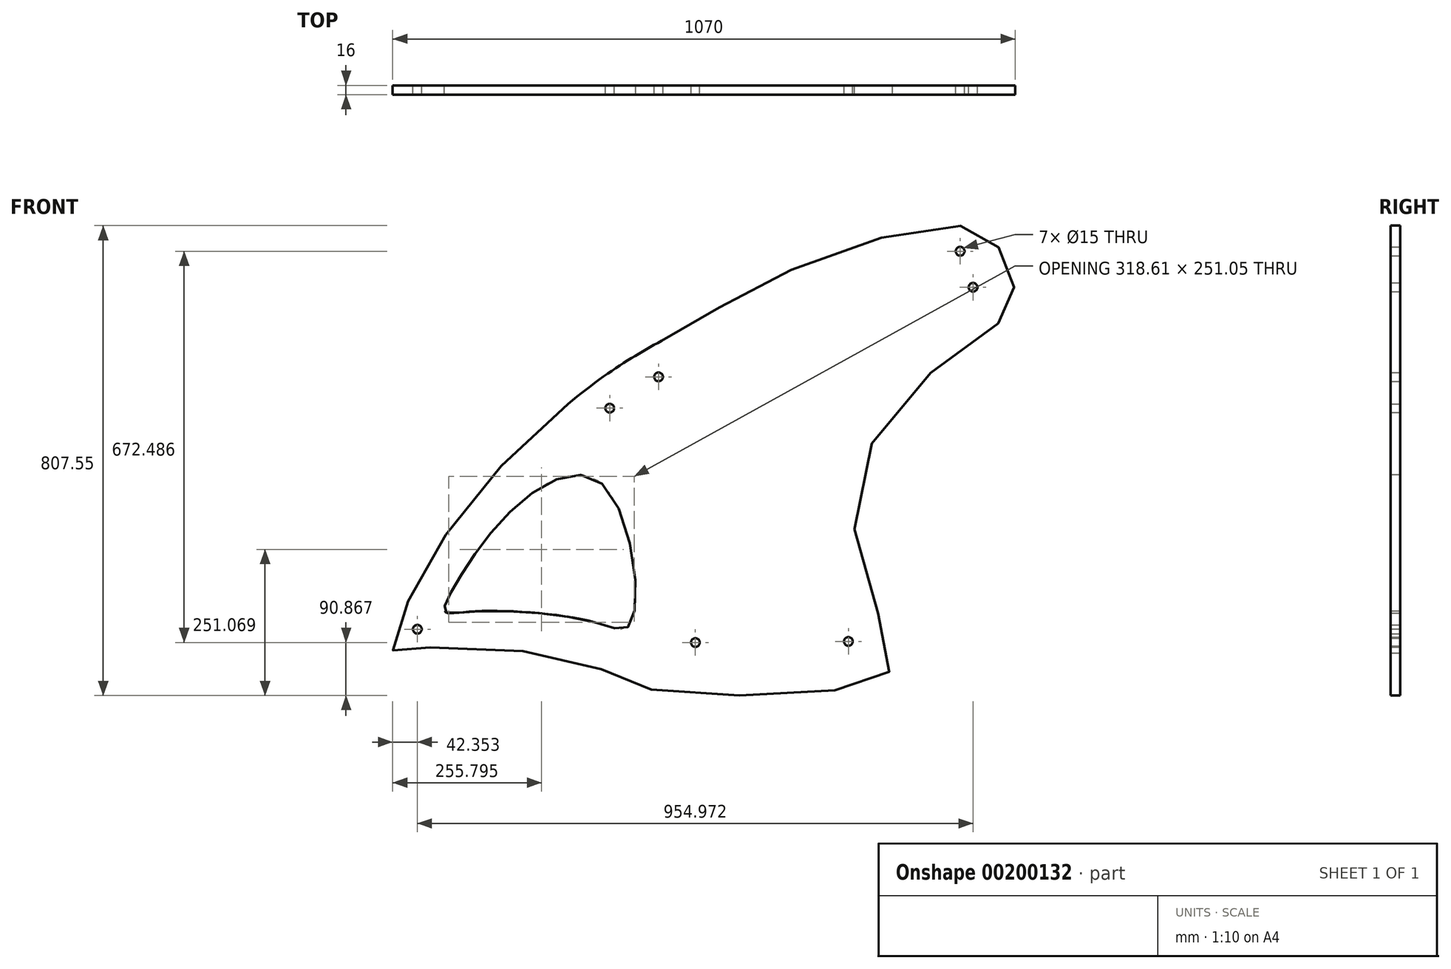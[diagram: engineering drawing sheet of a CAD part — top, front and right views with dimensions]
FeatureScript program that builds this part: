
annotation { "Feature Type Name" : "Feature", "Feature Type Description" : "" }
export const myFeature = defineFeature(function(context is Context, id is Id, definition is map)
    precondition{}
    {
        {
            var Q0;
            Q0=qCreatedBy(makeId("Front.planeOp"),FACE);
            var sketch = newSketch(context, id + "F0", { "sketchPlane" : qUnion([Q0])});
            skFitSpline(sketch, "E0", {"points": [v(296.8, 611.98) * mm, v(322.84, 547.63) * mm, v(318.6, 501.05) * mm, v(130.85, 348.58) * mm, v(56.03, 83.18) * mm, v(113.37, -111.05) * mm, v(0, -152.58) * mm, v(-308.6, -147.46) * mm, v(-413.67, -103.87) * mm, v(-700.28, -79.67) * mm, v(-741.76, -85.2) * mm, v(-720.02, -4.27) * mm, v(-590.43, 197.07) * mm, v(-376.55, 391.5) * mm, v(-238.95, 473.77) * mm, v(-38.49, 580.12) * mm, v(233.92, 647.2) * mm, v(296.8, 611.98) * mm]});
            skFitSpline(sketch, "E1", {"points": [v(-396.1, -34.16) * mm, v(-333.66, -35.6) * mm, v(-383.57, 203.97) * mm, v(-527.62, 168.65) * mm, v(-634.93, 31.23) * mm, v(-653.89, -14.93) * mm, v(-606.14, -15.45) * mm, v(-396.1, -34.16) * mm]});
            skFitSpline(sketch, "E2", {"points": [v(-423.1, 318.98) * mm, v(-514.85, 391.93) * mm, v(-576.24, 405.79) * mm, v(-634.5, 459.84) * mm, v(-484.83, 432.17) * mm, v(-242.1, 440.97) * mm, v(-245.01, 368.92) * mm, v(-319.45, 315.2) * mm, v(-394.83, 283.17) * mm, v(-423.1, 318.98) * mm]});
            skCircle(sketch, "E3", {"center": v(-700.99, -46.02) * mm, "radius": 12.5 * mm});
            skCircle(sketch, "E4", {"center": v(-700.99, -46.02) * mm, "radius": 7.5 * mm});
            skCircle(sketch, "E5", {"center": v(-223.24, -68.84) * mm, "radius": 12.5 * mm});
            skCircle(sketch, "E6", {"center": v(-223.24, -68.84) * mm, "radius": 7.5 * mm});
            skCircle(sketch, "E7", {"center": v(39.8, -66.94) * mm, "radius": 12.5 * mm});
            skCircle(sketch, "E8", {"center": v(39.8, -66.94) * mm, "radius": 7.5 * mm});
            skCircle(sketch, "E9", {"center": v(-370.33, 334.05) * mm, "radius": 12.5 * mm});
            skCircle(sketch, "E10", {"center": v(-370.33, 334.05) * mm, "radius": 7.5 * mm});
            skCircle(sketch, "E11", {"center": v(-286.47, 387.76) * mm, "radius": 12.5 * mm});
            skCircle(sketch, "E12", {"center": v(-286.47, 387.76) * mm, "radius": 7.5 * mm});
            skCircle(sketch, "E13", {"center": v(231.8, 603.64) * mm, "radius": 12.5 * mm});
            skCircle(sketch, "E14", {"center": v(231.8, 603.64) * mm, "radius": 7.5 * mm});
            skCircle(sketch, "E15", {"center": v(253.99, 541.84) * mm, "radius": 12.5 * mm});
            skCircle(sketch, "E16", {"center": v(253.99, 541.84) * mm, "radius": 7.5 * mm});
            skSolve(sketch);
        }
        {
            var Q0;
            Q0=makeQuery(id+"F0.imprint","IMPRINT",FACE,{"disambiguationData":[TD([[makeQuery(id+"F0.imprint","IMPRINT",EDGE,{"derivedFrom":sQuery(id+"F0.wireOp",EDGE,"E1")}),-1.0]])]});
            var Q1;
            Q1=makeQuery(id+"F0.imprint","IMPRINT",FACE,{"disambiguationData":[TD([[makeQuery(id+"F0.imprint","IMPRINT",EDGE,{"derivedFrom":sQuery(id+"F0.wireOp",EDGE,"E9")}),-1.0]])]});
            var Q2;
            Q2=makeQuery(id+"F0.imprint","IMPRINT",FACE,{"disambiguationData":[TD([[makeQuery(id+"F0.imprint","IMPRINT",EDGE,{"derivedFrom":sQuery(id+"F0.wireOp",EDGE,"E3")}),1.0]])]});
            var Q3;
            Q3=makeQuery(id+"F0.imprint","IMPRINT",FACE,{"disambiguationData":[TD([[makeQuery(id+"F0.imprint","IMPRINT",EDGE,{"derivedFrom":sQuery(id+"F0.wireOp",EDGE,"E5")}),1.0]])]});
            var Q4;
            Q4=makeQuery(id+"F0.imprint","IMPRINT",FACE,{"disambiguationData":[TD([[makeQuery(id+"F0.imprint","IMPRINT",EDGE,{"derivedFrom":sQuery(id+"F0.wireOp",EDGE,"E7")}),1.0]])]});
            var Q5;
            Q5=makeQuery(id+"F0.imprint","IMPRINT",FACE,{"disambiguationData":[TD([[makeQuery(id+"F0.imprint","IMPRINT",EDGE,{"derivedFrom":sQuery(id+"F0.wireOp",EDGE,"E11")}),1.0]])]});
            var Q6;
            Q6=makeQuery(id+"F0.imprint","IMPRINT",FACE,{"disambiguationData":[TD([[makeQuery(id+"F0.imprint","IMPRINT",EDGE,{"derivedFrom":sQuery(id+"F0.wireOp",EDGE,"E9")}),1.0]])]});
            var Q7;
            Q7=makeQuery(id+"F0.imprint","IMPRINT",FACE,{"disambiguationData":[TD([[makeQuery(id+"F0.imprint","IMPRINT",EDGE,{"derivedFrom":sQuery(id+"F0.wireOp",EDGE,"E13")}),1.0]])]});
            var Q8;
            Q8=makeQuery(id+"F0.imprint","IMPRINT",FACE,{"disambiguationData":[TD([[makeQuery(id+"F0.imprint","IMPRINT",EDGE,{"derivedFrom":sQuery(id+"F0.wireOp",EDGE,"E15")}),1.0]])]});
            extrude(context, id + "F1", {"entities" : qUnion([Q0, Q1, Q2, Q3, Q4, Q5, Q6, Q7, Q8]), "depth" : 16 * mm});
        }
    });
